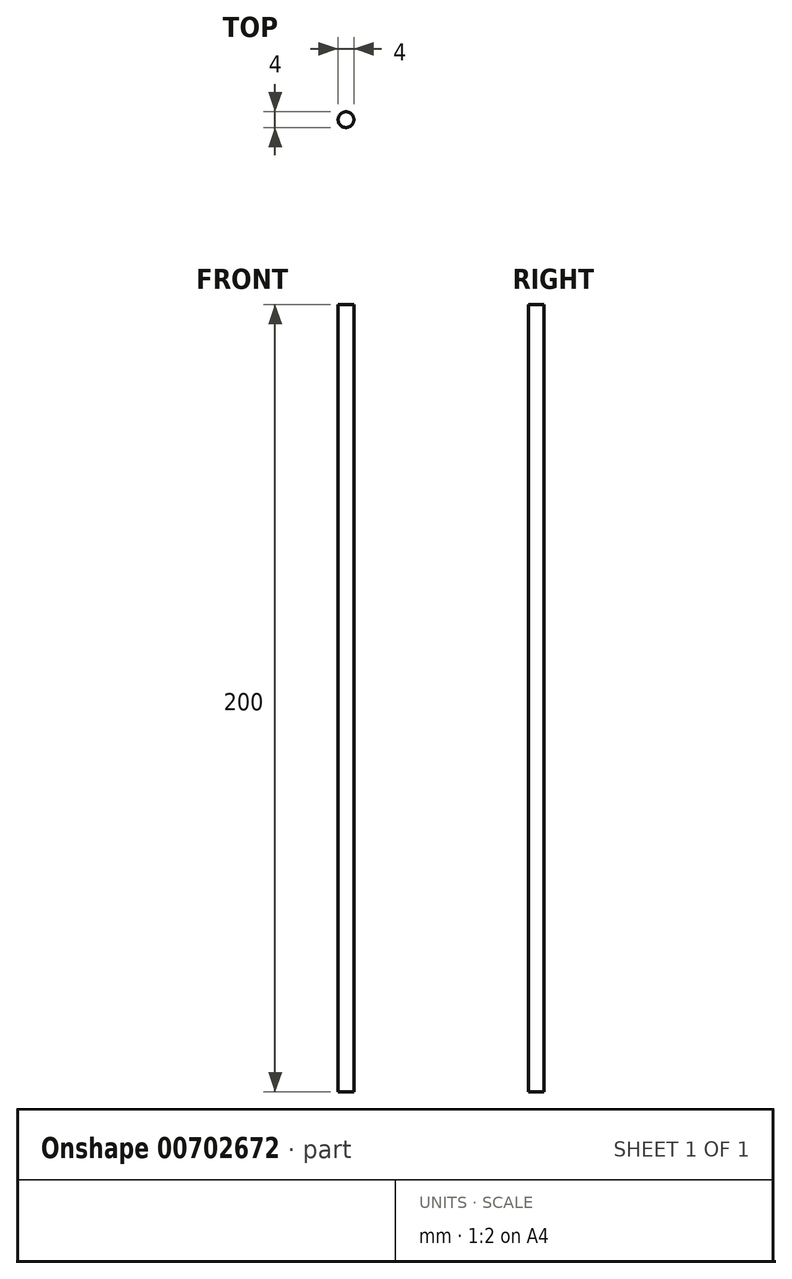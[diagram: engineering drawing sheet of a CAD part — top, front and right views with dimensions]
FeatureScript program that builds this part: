
annotation { "Feature Type Name" : "Feature", "Feature Type Description" : "" }
export const myFeature = defineFeature(function(context is Context, id is Id, definition is map)
    precondition{}
    {
        {
            var Q0;
            Q0=qCreatedBy(makeId("Top.planeOp"),FACE);
            var sketch = newSketch(context, id + "F0", { "sketchPlane" : qUnion([Q0])});
            skCircle(sketch, "E0", {"center": v(0, 0) * mm, "radius": 2 * mm});
            skSolve(sketch);
        }
        {
            var Q0;
            Q0 = qSketchRegion(id + "F0", true);
            extrude(context, id + "F1", {"entities" : qUnion([Q0]), "depth" : 200 * mm, "offsetDistance" : 25 * mm});
        }
    });
